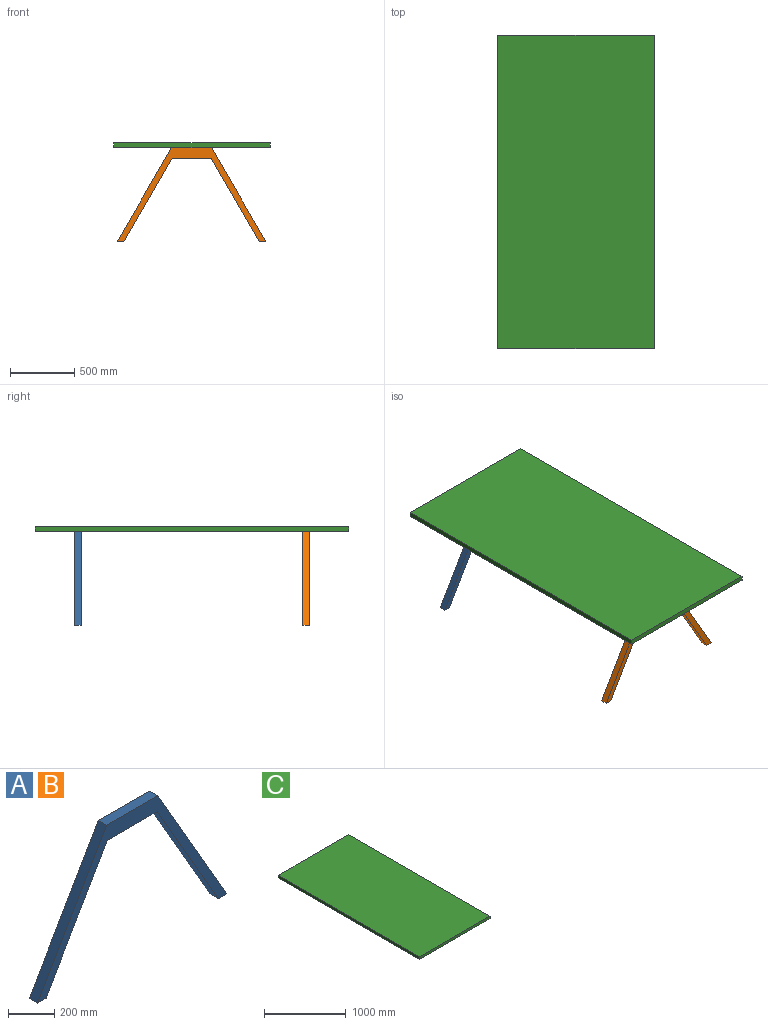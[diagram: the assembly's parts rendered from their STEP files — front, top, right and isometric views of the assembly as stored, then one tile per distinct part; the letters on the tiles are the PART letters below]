
ASSEMBLY  parts=3 mates=2
PART A: 10 faces, bbox 1155.7x50.8x731.3 mm
  f0: plane 731.3x421.4mm, normal (-0.87,0,0.5), area 42876.4mm2, adj f1,f7,f8,f9
  f1: plane 50.8x50.8mm, normal (0,0,-1), area 2580.6mm2, adj f0,f2,f8,f9
  f2: plane 648.91x374.65mm, normal (0.87,0,-0.5), area 38064.4mm2, adj f1,f3,f8,f9
  f3: plane 304.8x50.8mm, normal (0,0,-1), area 15483.8mm2, adj f2,f4,f8,f9
  f4: plane 648.91x374.65mm, normal (-0.87,0,-0.5), area 38064.4mm2, adj f3,f5,f8,f9
  f5: plane 50.8x50.8mm, normal (0,0,-1), area 2580.6mm2, adj f4,f6,f8,f9
  f6: plane 731.3x422.22mm, normal (0.87,0,0.5), area 42897.1mm2, adj f5,f7,f8,f9
  f7: plane 312.09x50.8mm, normal (0,0,1), area 15854mm2, adj f0,f6,f8,f9
  f8: plane 1155.7x731.3mm, normal (0,-1,0), area 95791.7mm2, adj f0,f1,f2,f3,f4,f5,f6,f7
  f9: plane 1155.7x731.3mm, normal (0,1,0), area 95791.7mm2, adj f0,f1,f2,f3,f4,f5,f6,f7
PART B: same geometry as A
PART C: 6 faces, bbox 1219.2x2438.4x38.1 mm
  f0: plane 1219.2x38.1mm, normal (0,1,0), area 46451.5mm2, adj f1,f3,f4,f5
  f1: plane 2438.4x38.1mm, normal (-1,0,0), area 92903mm2, adj f0,f2,f4,f5
  f2: plane 1219.2x38.1mm, normal (0,-1,0), area 46451.5mm2, adj f1,f3,f4,f5
  f3: plane 2438.4x38.1mm, normal (1,0,0), area 92903mm2, adj f0,f2,f4,f5
  f4: plane 2438.4x1219.2mm, normal (0,0,1), area 2972897.3mm2, adj f0,f1,f2,f3
  f5: plane 2438.4x1219.2mm, normal (0,0,-1), area 2972897.3mm2, adj f0,f1,f2,f3
PLACE A t=(-595.41,1074.69,-273.99)mm
PLACE B t=(-595.41,-703.31,-273.99)mm
PLACE C t=(164.91,-778.93,345.59)mm
MATE fastened B.f7 <-> C.f5  axis (0,0,1) through (8.98,-754.11,345.59)mm
MATE fastened A.f7 <-> C.f5  axis (0,0,1) through (8.98,1074.69,345.59)mm
